# Revit family: IS_ConnectBlue_B9917_BIM_DE
name_source: partatom
category: Plumbing Fixtures
revit_build: Autodesk Revit MEP 2014 (Build: 20130308_1515(x64)
units: mm (PartAtom-declared; Revit-internal decimal feet)

## types (1)
- B9917AA - Connect Blue single lever basin mixer no pop-up waste
    Accessories = www.idealstandard.de\ersatzteile
    AreaUnits = millimeters
    Assembly Code = C1030200
    AssetType = Fixed
    BIMObjectName = ISI_IdealStandard_WashBasinTaps_ConnectBlue_B9917AA
    BarCode = 3800861031499
    Brand = Ideal Standard
    CWFU = 0
    CodePerformance = EN 817, DIN 4109
    Color = chrome
    ConnectionType = Plumbing
    Cost = 0 $
    Default Elevation = 800 mm  [stored 2.62467 ft]
    Description = B9917AA Connect Blue single lever basin mixer no pop-up waste
    DurationUnit = year
    ExpectedLife = 25
    FaucetFunction = MIXED
    FaucetOperation = LEVERHANDLE
    FaucetType = PILLAR
    Features = Connect Blue single lever basin mixer no pop-up waste
    Finish = chrome
    FlowRate = 11 Liters @ 3bar
    GrossWeight = 0
    HWFU = 0
    IfcExportAs = IfcValveType
    IfcExportType = FAUCET
    InstallationInstructions = www.idealstandard.de\produkte
    LinearUnits = millimeters
    ManufacturerURL = www.idealstandard.de
    Material = Brass
    Model = B9917AA
    ModelNumber = B9917AA
    ModelReference = B9917AA Connect Blue single lever basin mixer no pop-up waste
    NBSDescription = Water supply fittings for wash basins and troughs
    NBSReference = 45-35-70/371
    Name = WashBasinTaps_ConnectBlue_B9917AA_IdealStandard
    NettWeight = 1,586 kg
    NominalHeight = 166 mm
    NominalLength = 146 mm
    NominalWidth = 51 mm  [stored 0.167323 ft]
    ProductInformation = www.idealstandard.de/produkte
    Shape = Sculptured
    Size = 70x168x410mm
    Space = Internal
    SpareParts = www.idealstandard.de/ersatzteile
    TMV3 = No
    TestPressure = 10 Bar
    URL = www.idealstandard.com
    Uniclass2015Code = Pr_40_20_87_98
    Uniclass2015Title = Wash basin taps
    Uniclass2015Version = Products v1.1
    ValveMechanism = i.e.ceramic disc
    ValveOperation = i.e.lever
    Version = 2
    VolumeUnits = Litres
    WFU = 0
    WarrantyDescription = Manufacturers Warranty
    WarrantyDurationUnit = year
    WorkingPressure = 1-5 Bar

note: [stored X ft] marks values corroborated as IEEE doubles in the binary element streams (Revit-internal decimal feet)

## geometry (parser evidence)
native form markers: Sweep x2
no freeform markers — native parametric forms only
